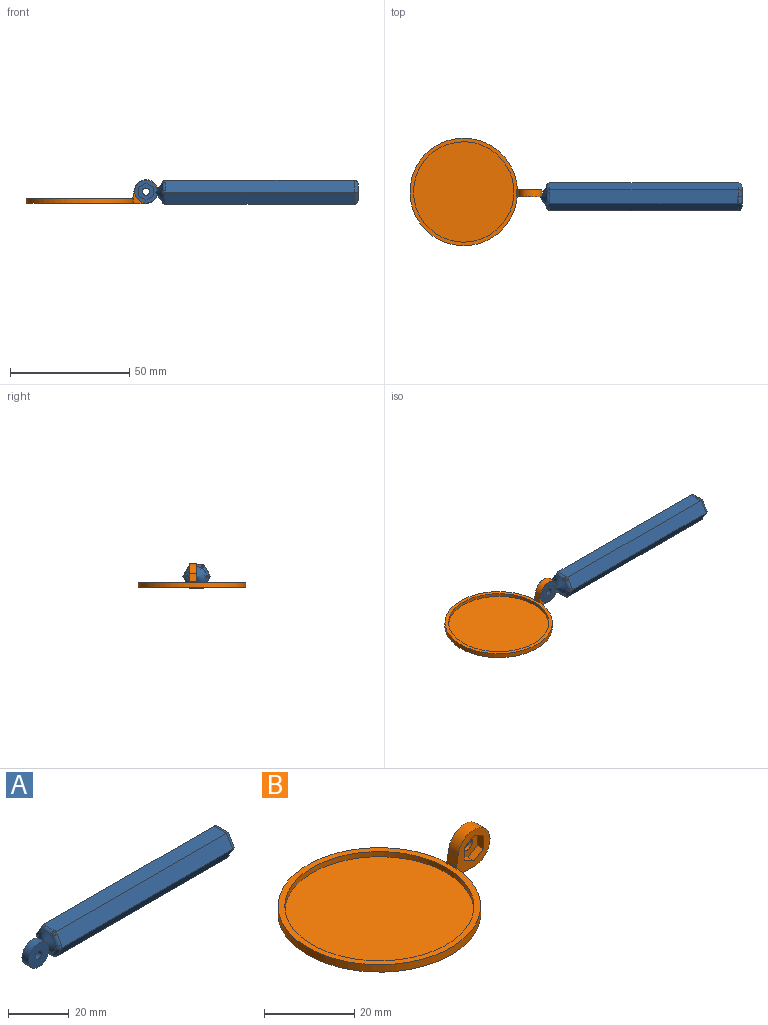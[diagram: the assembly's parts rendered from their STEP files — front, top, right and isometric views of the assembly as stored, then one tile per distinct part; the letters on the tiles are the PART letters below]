
ASSEMBLY  parts=2 mates=1
PART A: 53 faces, bbox 93.5x11.6x10 mm
  f0: plane 0.13x0.07mm, normal (-1,0,0), area 0mm2, adj f1,f38,f39
  f1: cylinder r=1.5mm len=1.77mm, axis (0,0.5,-0.87), area 1.5mm2, adj f0,f2,f37,f38
  f2: plane 79.09x5mm, normal (0,-0.87,-0.5), area 456.3mm2, adj f1,f3,f34,f35,f36,f37
  f3: cylinder r=1.5mm len=1.77mm, axis (0,0.5,-0.87), area 1.5mm2, adj f2,f4,f5,f37
  f4: plane 0.15x0.04mm, normal (-1,0,0), area 0mm2, adj f3,f5,f39
  f5: cylinder r=1.5mm len=1.77mm, axis (0,-0.5,-0.87), area 1.5mm2, adj f3,f4,f6,f34
  f6: bspline ~4.77x3.69mm, area 7.8mm2, adj f5,f7,f34,f39
  f7: cylinder r=1.5mm len=1.77mm, axis (0,-0.5,-0.87), area 1.5mm2, adj f6,f8,f9,f34
  f8: plane 0.13x0.07mm, normal (-1,0,0), area 0mm2, adj f7,f9,f39
  f9: cylinder r=1.5mm len=1.5mm, axis (0,-1,0), area 1.5mm2, adj f7,f8,f10,f33
  f10: bspline ~4.68x1.79mm, area 7.8mm2, adj f9,f11,f33,f39
  f11: cylinder r=1.5mm len=1.5mm, axis (0,-1,0), area 1.5mm2, adj f10,f12,f13,f33
  f12: plane 0.13x0.07mm, normal (-1,0,0), area 0mm2, adj f11,f13,f39
  f13: cylinder r=1.5mm len=1.77mm, axis (0,-0.5,0.87), area 1.5mm2, adj f11,f12,f14,f32
  f14: bspline ~4.8x3.77mm, area 7.8mm2, adj f13,f15,f32,f39
  f15: cylinder r=1.5mm len=1.77mm, axis (0,-0.5,0.87), area 1.5mm2, adj f14,f16,f17,f32
  f16: plane 0.15x0.04mm, normal (-1,0,0), area 0mm2, adj f15,f17,f39
  f17: cylinder r=1.5mm len=1.77mm, axis (0,0.5,0.87), area 1.5mm2, adj f15,f16,f18,f23
  f18: bspline ~4.1x3.24mm, area 7.8mm2, adj f17,f19,f23,f39
  f19: cylinder r=1.5mm len=1.77mm, axis (0,0.5,0.87), area 1.5mm2, adj f18,f20,f21,f23
  f20: plane 0.13x0.07mm, normal (-1,0,0), area 0mm2, adj f19,f21,f39
  f21: cylinder r=1.5mm len=1.5mm, axis (0,1,0), area 1.5mm2, adj f19,f20,f22,f36
  f22: bspline ~4.68x1.79mm, area 7.8mm2, adj f21,f36,f38,f39
  f23: plane 79.09x5mm, normal (0,0.87,-0.5), area 456.3mm2, adj f17,f18,f19,f24,f31,f32,f36
  f24: plane 2.89x0.51mm, normal (0,0,-1), area 1.4mm2, adj f23,f25,f36
  f25: cylinder r=1.5mm len=2.88mm, axis (0,-1,0), area 5.8mm2, adj f24,f26,f27,f31
  f26: cylinder r=1.5mm len=2.89mm, axis (0,-1,0), area 5.8mm2, adj f25,f27,f35,f36
  f27: plane 8.08x7mm, normal (1,0,0), area 42.4mm2, adj f25,f26,f28,f29,f30,f31,f35
  f28: cylinder r=1.5mm len=5.78mm, axis (0,1,0), area 11.6mm2, adj f27,f29,f30,f33
  f29: cylinder r=1.5mm len=5.75mm, axis (0,0.5,-0.87), area 11.6mm2, adj f27,f28,f31,f32
  f30: cylinder r=1.5mm len=5.75mm, axis (0,0.5,0.87), area 11.6mm2, adj f27,f28,f34,f35
  f31: cylinder r=1.5mm len=5.74mm, axis (0,-0.5,-0.87), area 11.6mm2, adj f23,f25,f27,f29
  f32: plane 79.09x5mm, normal (0,0.87,0.5), area 456.3mm2, adj f13,f14,f15,f23,f29,f33
  f33: plane 79.09x5.77mm, normal (0,0,1), area 456.3mm2, adj f9,f10,f11,f28,f32,f34
  f34: plane 79.09x5mm, normal (0,-0.87,0.5), area 456.3mm2, adj f2,f5,f6,f7,f30,f33
  f35: cylinder r=1.5mm len=5.75mm, axis (0,-0.5,0.87), area 11.6mm2, adj f2,f26,f27,f30
  f36: plane 79.09x5.78mm, normal (0,0,-1), area 454.8mm2, adj f2,f21,f22,f23,f24,f26,f38
  f37: bspline ~4.8x3.77mm, area 7.8mm2, adj f1,f2,f3,f39
  f38: cylinder r=1.5mm len=1.5mm, axis (0,1,0), area 1.5mm2, adj f0,f1,f22,f36
  f39: cone r=4mm half-angle=56deg, axis (1,0,0), area 60.6mm2, adj f0,f4,f6,f8,f10,f12,f14,f16
  f40: plane 6.93x6.05mm, normal (-1,0,0), area 31.2mm2, adj f42,f43,f44,f45,f46,f47
  f41: plane 6.93x6.05mm, normal (1,0,0), area 31.2mm2, adj f42,f43,f44,f45,f46,f47
  f42: plane 80x3.02mm, normal (0,0.87,-0.49), area 277.1mm2, adj f40,f41,f43,f47
  f43: plane 80x2.98mm, normal (0,0.86,0.51), area 277.1mm2, adj f40,f41,f42,f44
  f44: plane 80x3.46mm, normal (0,-0.01,1), area 277.1mm2, adj f40,f41,f43,f45
  f45: plane 80x3.02mm, normal (0,-0.87,0.49), area 277.1mm2, adj f40,f41,f44,f46
  f46: plane 80x2.98mm, normal (0,-0.86,-0.51), area 277.1mm2, adj f40,f41,f45,f47
  f47: plane 80x3.46mm, normal (0,0.01,-1), area 277.1mm2, adj f40,f41,f42,f46
  f48: cylinder r=4.75mm len=9.5mm, axis (0,1,0), area 89.5mm2, adj f49,f50,f51
  f49: plane 9.5x9.5mm, normal (0,-1,0), area 63.3mm2, adj f48,f52
  f50: plane 9.5x9.45mm, normal (0,1,0), area 62.7mm2, adj f48,f51,f52
  f51: cone r=4mm half-angle=56deg, axis (1,0,0), area 1.5mm2, adj f48,f50
  f52: cylinder r=1.55mm len=3.1mm, axis (0,1,0), area 29.2mm2, adj f49,f50
PART B: 20 faces, bbox 55.2x45x10 mm
  f0: cylinder r=21mm len=42mm, axis (0,0,-1), area 184.7mm2, adj f2,f3
  f1: cylinder r=22.5mm len=45mm, axis (0,0,-1), area 276.7mm2, adj f2,f4,f7,f12
  f2: plane 45x44.98mm, normal (0,0,1), area 204.2mm2, adj f0,f1,f7,f10,f12
  f3: plane 42x42mm, normal (0,0,1), area 1385.4mm2, adj f0
  f4: plane 45x44.98mm, normal (0,0,-1), area 1589.6mm2, adj f1,f5,f7,f12
  f5: plane 3x0.03mm, normal (-1,0,0), area 0.1mm2, adj f4,f7,f11,f12
  f6: cylinder r=1.5mm len=3mm, axis (0,-1,0), area 9.4mm2, adj f12,f19
  f7: plane 10.52x9.98mm, normal (0,-1,0), area 53.5mm2, adj f1,f2,f4,f5,f8,f9,f10,f11
  f8: cylinder r=5mm len=9.98mm, axis (0,-1,0), area 66.6mm2, adj f7,f9,f11,f12
  f9: plane 3.34x3mm, normal (-0.98,0,0.18), area 10.2mm2, adj f7,f8,f10,f12
  f10: plane 3x0.48mm, normal (-1,0,0), area 1.4mm2, adj f2,f7,f9,f12
  f11: plane 6.01x3mm, normal (0,0,-1), area 18mm2, adj f5,f7,f8,f12
  f12: plane 10.52x9.98mm, normal (0,1,0), area 78.2mm2, adj f1,f2,f4,f5,f6,f8,f9,f10
  f13: plane 3.04x2mm, normal (-0.5,0,-0.87), area 7mm2, adj f7,f14,f18,f19
  f14: plane 3.04x2mm, normal (0.5,0,-0.87), area 7mm2, adj f7,f13,f15,f19
  f15: plane 3.51x2mm, normal (1,0,0), area 7mm2, adj f7,f14,f16,f19
  f16: plane 3.04x2mm, normal (0.5,0,0.87), area 7mm2, adj f7,f15,f17,f19
  f17: plane 3.04x2mm, normal (-0.5,0,0.87), area 7mm2, adj f7,f16,f18,f19
  f18: plane 3.51x2mm, normal (-1,0,0), area 7mm2, adj f7,f13,f17,f19
  f19: plane 7.01x6.07mm, normal (0,-1,0), area 24.9mm2, adj f6,f13,f14,f15,f16,f17,f18
PLACE A rot(axis=(1,0,0),180deg) t=(-54.05,2.79,27.03)mm
PLACE B t=(-60.23,4.79,0.43)mm
MATE revolute A.f48 <-> B.f6  axis (0,1,0) through (-32.5,5.79,4.77)mm
